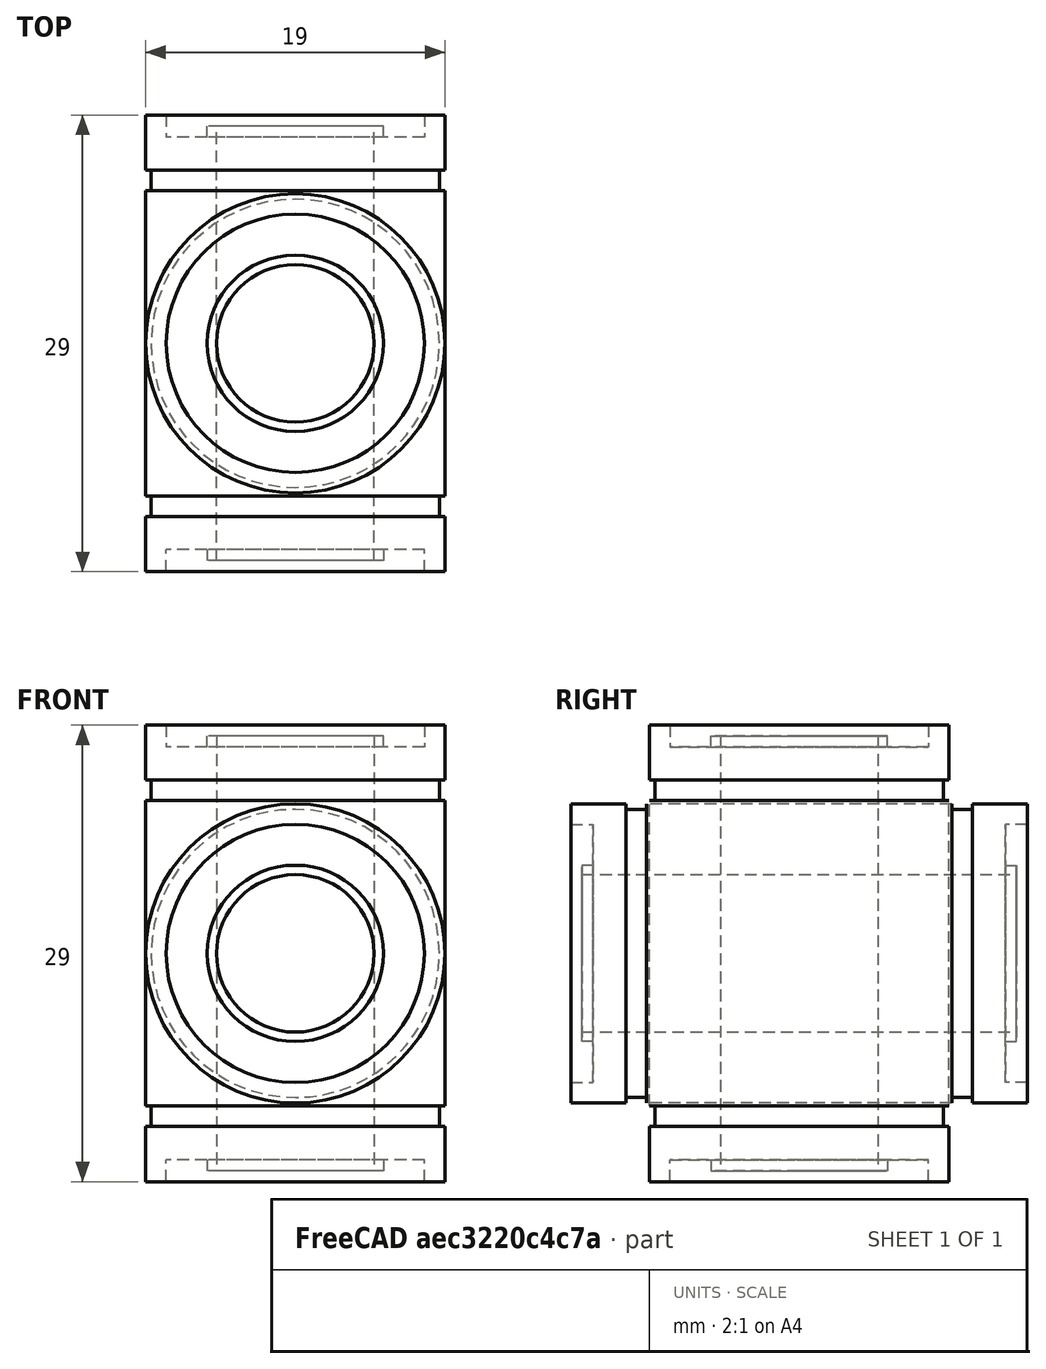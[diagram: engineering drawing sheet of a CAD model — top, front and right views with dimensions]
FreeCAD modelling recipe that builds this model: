
FCSTD DOCUMENT  (FreeCAD 0.16R6706 (Git))
Label: LM10uu
License: CreativeCommons Attribution-ShareAlike
LicenseURL: http://creativecommons.org/licenses/by-sa/4.0/
objects: Sketcher::SketchObject×1, PartDesign::Revolution×1, Part::Feature×1
note: 4 computed .brp shape members not serialized (recipe doc carries the construction recipe); baked Part::Feature solids carry a one-line shape summary decoded from their .brp

FEATURE [Sketcher::SketchObject] Sketch  label="lm10uu-cross-section"
  Placement = pos=(0,0,0) rot=(1,0,0;1.5708rad)
  sketch-geometry (20):
    g0: LineSegment StartX=9.5 StartY=-14.5 StartZ=0 EndX=9.5 EndY=-11 EndZ=0
    g1: LineSegment StartX=9.5 StartY=9.7 StartZ=0 EndX=9.15 EndY=9.7 EndZ=0
    g2: LineSegment StartX=9.15 StartY=9.7 StartZ=0 EndX=9.15 EndY=11 EndZ=0
    g3: LineSegment StartX=9.15 StartY=11 StartZ=0 EndX=9.5 EndY=11 EndZ=0
    g4: LineSegment StartX=9.5 StartY=11 StartZ=0 EndX=9.5 EndY=14.5 EndZ=0
    g5: LineSegment StartX=9.5 StartY=14.5 StartZ=0 EndX=8.2 EndY=14.5 EndZ=0
    g6: LineSegment StartX=8.2 StartY=14.5 StartZ=0 EndX=8.2 EndY=13.1 EndZ=0
    g7: LineSegment StartX=8.2 StartY=13.1 StartZ=0 EndX=5.6 EndY=13.1 EndZ=0
    g8: LineSegment StartX=5.6 StartY=13.1 StartZ=0 EndX=5.6 EndY=13.8 EndZ=0
    g9: LineSegment StartX=5.6 StartY=13.8 StartZ=0 EndX=5 EndY=13.8 EndZ=0
    g10: LineSegment StartX=5 StartY=13.8 StartZ=0 EndX=5 EndY=-13.8 EndZ=0
    g11: LineSegment StartX=9.5 StartY=-9.7 StartZ=0 EndX=9.15 EndY=-9.7 EndZ=0
    g12: LineSegment StartX=9.15 StartY=-11 StartZ=0 EndX=9.5 EndY=-11 EndZ=0
    g13: LineSegment StartX=9.5 StartY=-9.7 StartZ=0 EndX=9.5 EndY=9.7 EndZ=0
    g14: LineSegment StartX=9.15 StartY=-9.7 StartZ=0 EndX=9.15 EndY=-11 EndZ=0
    g15: LineSegment StartX=9.5 StartY=-14.5 StartZ=0 EndX=8.2 EndY=-14.5 EndZ=0
    g16: LineSegment StartX=8.2 StartY=-14.5 StartZ=0 EndX=8.2 EndY=-13.1 EndZ=0
    g17: LineSegment StartX=8.2 StartY=-13.1 StartZ=0 EndX=5.6 EndY=-13.1 EndZ=0
    g18: LineSegment StartX=5.6 StartY=-13.1 StartZ=0 EndX=5.6 EndY=-13.8 EndZ=0
    g19: LineSegment StartX=5.6 StartY=-13.8 StartZ=0 EndX=5 EndY=-13.8 EndZ=0
  constraints (58):
    c: Coincident(g13,g1)
    c: Coincident(g1,g2)
    c: Vertical(g2)
    c: Coincident(g2,g3)
    c: Coincident(g3,g4)
    c: Vertical(g4)
    c: Coincident(g4,g5)
    c: Coincident(g5,g6)
    c: Vertical(g6)
    c: Coincident(g6,g7)
    c: Horizontal(g7)
    c: Coincident(g7,g8)
    c: Vertical(g8)
    c: Coincident(g8,g9)
    c: Horizontal(g9)
    c: Coincident(g9,g10)
    c: Vertical(g10)
    c: Horizontal(g1)
    c: Horizontal(g5)
    c: Horizontal(g3)
    c: PointOnObject(g3,g0)
    c: Symmetric(g0,g4,g-1)
    c: DistanceY(g4,g0) = -29
    c: DistanceY(g2) = 1.3
    c: DistanceX(g3) = 0.35
    c: DistanceX(g-1,g4) = 9.5
    c: DistanceX(g-1,g9) = 5
    c: DistanceX(g5) = -1.3
    c: DistanceX(g9) = -0.6
    c: DistanceY(g6) = -1.4
    c: DistanceY(g8) = 0.7
    c: Horizontal(g11)
    c: Horizontal(g12)
    c: Coincident(g13,g11)
    c: Tangent(g0,g13)
    c: Coincident(g12,g0)
    c: PointOnObject(g14,g11)
    c: Coincident(g14,g12)
    c: Vertical(g14)
    c: Symmetric(g1,g11,g-1)
    c: DistanceY(g13) = 19.4
    c: Equal(g14,g2)
    c: Coincident(g0,g15)
    c: Horizontal(g15)
    c: Coincident(g15,g16)
    c: Vertical(g16)
    c: Coincident(g16,g17)
    c: Horizontal(g17)
    c: Coincident(g17,g18)
    c: Vertical(g18)
    c: Coincident(g18,g19)
    c: Horizontal(g19)
    c: Coincident(g10,g19)
    c: Symmetric(g10,g9,g-1)
    c: Symmetric(g16,g6,g-1)
    c: Symmetric(g17,g7,g-1)
    c: Coincident(g14,g11)
    c: PointOnObject(g11,g2)
FEATURE [PartDesign::Revolution] Revolution  label="LM10uu"
  Angle = 360
  Axis = (0,0,1)
  Base = (0,0,0)
  Placement = pos=(0,0,0) rot=(1,0,0;1.5708rad)
  ReferenceAxis = -> Sketch [V_Axis]
  Reversed = true
  Sketch = -> Sketch
FEATURE [Part::Feature] Revolution001  label="LM10uu001"
  Placement = pos=(0,0,0) rot=(1,0,0;1.5708rad)
  shape: bbox 19 x 29 x 19 mm, 20 faces (baked)
